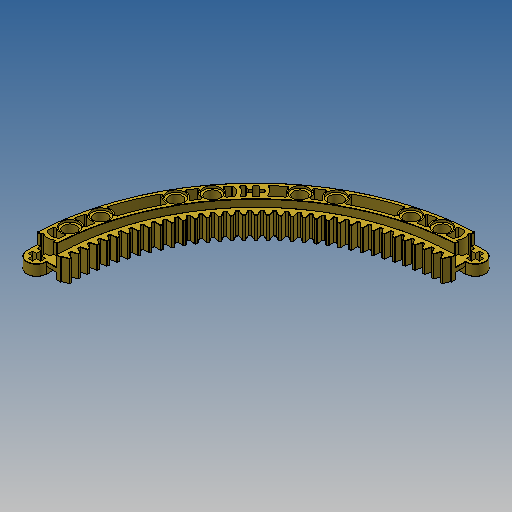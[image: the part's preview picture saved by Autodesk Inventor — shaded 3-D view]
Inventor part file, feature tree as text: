
AUTODESK INVENTOR PART (.ipt)
format: ipt  version: 2025 (Build 290162010, 162A)  size: 1,544,192 bytes
history: native  units: in
note: dims shown in document units (in); Inventor stores cm internally (conversion verified against a paired STEP export)
features: extrude x5, fillet x2, sketch x1, pattern_circular x1
ambient origin geometry x8: Origin, YZ Plane, XZ Plane, XY Plane, X Axis, Y Axis, Z Axis, Center Point
bodies: Solid1 (feature_tree)
feature tree (9):
  sketch  "Sketch2"  dims[d0=3.1496in d1=0.189in d2=0.2835in d3=0.189in d4=0.252in d5=0.315in d6=0.315in d8=45.0deg d10=0.4454in d11=0.4454in d12=0.1417in d13=0.0494in d14=0.0494in d15=0.0494in d16=0.1594in d17=0.1594in d18=0.1594in d19=0.063in d20=0.063in d21=0.4454in d22=2.8035in d23=2.8661in d24=0.0611in d25=0.0787in d26=0.0315in d27=0.0945in d28=0.1575in d29=0.0in d30=0.1575in d31=0.0in d32=0.063in d33=0.0in d34=0.252in d35=0.0in d36=0.315in d37=0.0in d38=0.0039in d39=13.7795in d40=0.6008in d42=0.063in d43=0.0039in d44=0.0157in d45=3.7795in]
  extrude  "Extrusion1"  Depth=0.0157in
  extrude  "Extrusion2"  Depth=0.0157in
  extrude  "Extrusion3"  Depth=0.0157in
  extrude  "Extrusion4"  Depth=0.0157in
  extrude  "Extrusion5"  Depth=0.0157in
  fillet  "Fillet1"  Radius=0.315in
  pattern_circular  "Circular Pattern1"  Angle=45.0deg  [1 undecoded]
  fillet  "Fillet2"  Radius=0.4454in
note: 1 required parameter value undecoded (feature->parameter linkage not recoverable at this tier; creation-order binding heuristic only, values carry confidence <= 0.55)
